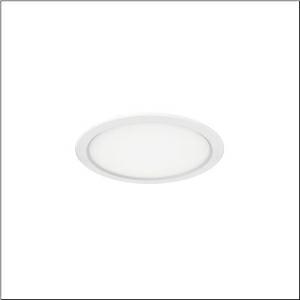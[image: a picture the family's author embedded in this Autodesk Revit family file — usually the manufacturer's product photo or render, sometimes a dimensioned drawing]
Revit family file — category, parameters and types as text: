
# Revit family: lunis_41_eco_51ds107f44b
name_source: partatom
category: Lighting Fixtures
units: mm (PartAtom-declared; Revit-internal decimal feet)

## family parameters
Cut with Voids When Loaded = No
Host = Face
Light Source = No
Part Type = Normal
Room Calculation Point = No
Round Connector Dimension = Use Diameter
Shared = No

## types (1)
- Lunis 41 Eco (1 x LED, 2300 lm, 17.5 W, 4000K)
    Apparent Load = 18 VA
    CIE Flux Codes = 47 80 97 100 100
    Color Rendering = 80
    Color Temperature = 4000K
    Default Elevation = 1800 mm
    Description = Lunis 41,  Eco, downlight, light emission: direct distribution, LED rated luminous flux: 2.300lm, light colour: 840, mains connection: 230V, AC, 50/60Hz, housing, round, of aluminium, coated, traffic white (RAL 9016), diameter: 216mm, recess depth: 58mm, protection rating (complete): IP20, protection rating (on room side): IP40, insulation class (complete): insulation class II (safety insulation), certification: CE, permissible ambient temperature for indoor applications: -20..+40°C, packaging unit: 1 piece
    Height = 0 mm  [stored 0 ft]
    Lamp = 1 x LED
    Lamp Light Flux = 2300 lm
    Lamp Power = 17.5 W
    Lamp count = 1
    Length = 216 mm
    Luminous efficacy = 131 lm/W
    Manufacturer = Siteco
    ModVariant = No
    Model = 51DS107F44B
    Mounting Place = Ceiling
    Mounting Type = Recessed
    Number of Poles = 1
    OnlyDefault = Yes
    Power Factor = 1
    Product Name = Lunis 41 Eco
    Product group = downlight
    ProductGroupID = 401
    Protection Class = Protection class II
    Protection Degree = IP 20
    RLX_Detail_Level = 1
    RLX_Emergency_Light_Flux = 0 lm
    RLX_Emergency_Type = 0
    RLX_Emergency_Type_DB = No
    RlxData = <blob elided: 10229 chars, md5=ff5d2100>
    Socket = socket
    Standby Power = 0 W
    System Light Flux = 2300 lm
    System Power = 18 W
    Type Comments = Product without accessories
    Type Image = l_1345914.jpg
    URL = http://relux.com
    VarID = ---
    Voltage = 0 V
    Weight = 0.00 kg
    Width = 0 mm  [stored 0 ft]

note: [stored X ft] marks values corroborated as IEEE doubles in the binary element streams (Revit-internal decimal feet)

## geometry (parser evidence)
native form markers: Sweep x9
no freeform markers — native parametric forms only
